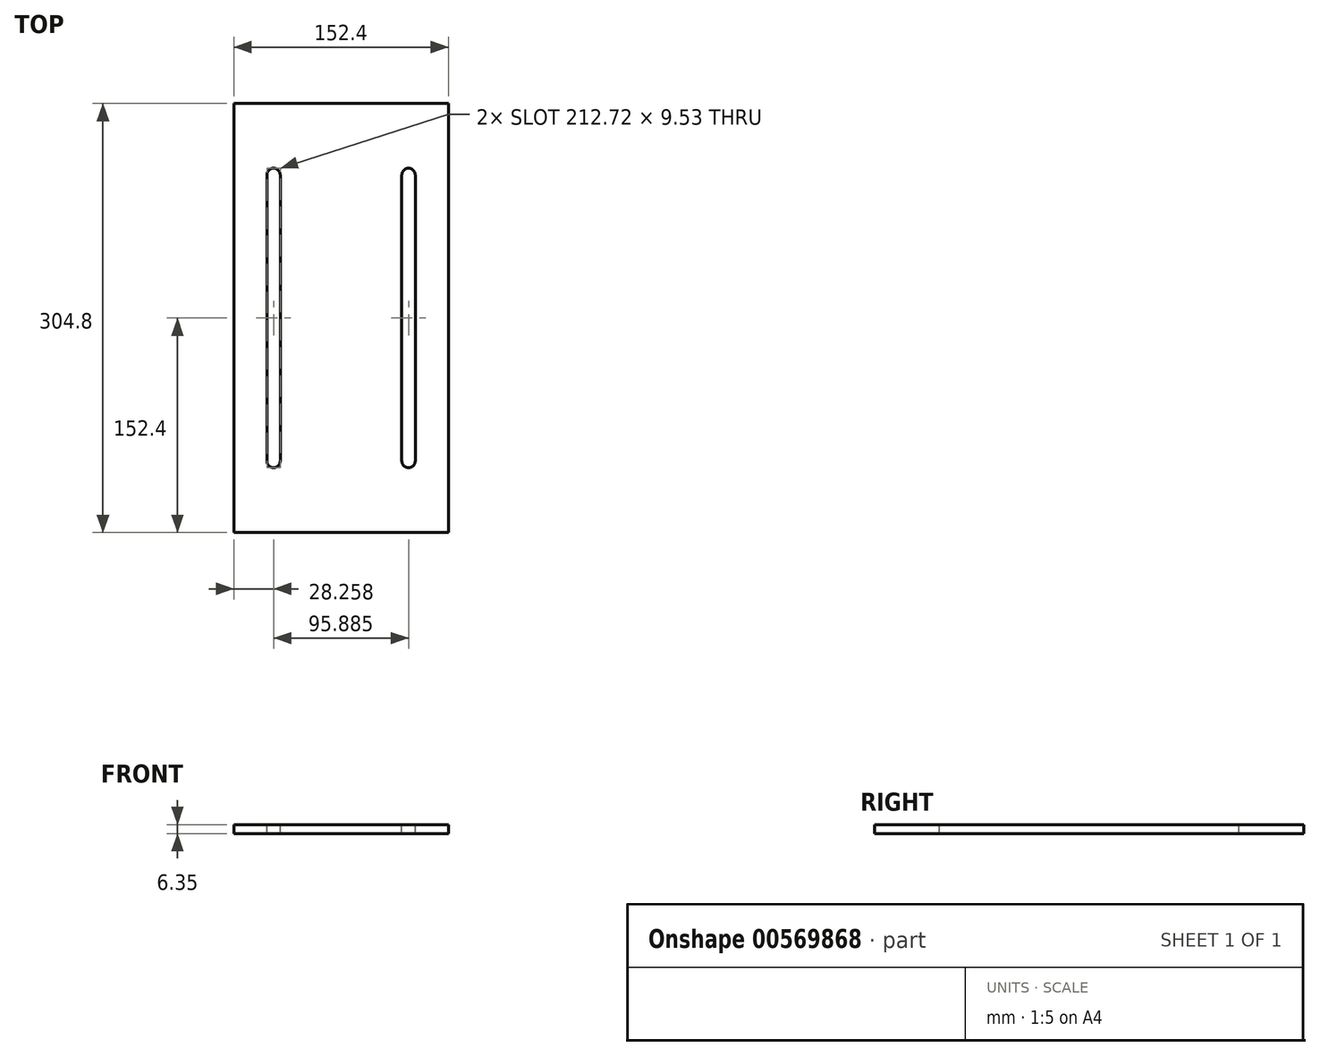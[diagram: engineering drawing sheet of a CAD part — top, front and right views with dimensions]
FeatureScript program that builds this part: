
annotation { "Feature Type Name" : "Feature", "Feature Type Description" : "" }
export const myFeature = defineFeature(function(context is Context, id is Id, definition is map)
    precondition{}
    {
        {
            var Q0;
            Q0=qCreatedBy(makeId("Top.planeOp"),FACE);
            var sketch = newSketch(context, id + "F0", { "sketchPlane" : qUnion([Q0])});
            skLineSegment(sketch, "E0.bottom", {"start": v(0, 0) * mm, "end": v(-152.4, 0) * mm});
            skLineSegment(sketch, "E0.top", {"start": v(0, 304.8) * mm, "end": v(-152.4, 304.8) * mm});
            skLineSegment(sketch, "E0.left", {"start": v(0, 0) * mm, "end": v(0, 304.8) * mm});
            skLineSegment(sketch, "E0.right", {"start": v(-152.4, 0) * mm, "end": v(-152.4, 304.8) * mm});
            skSolve(sketch);
        }
        {
            var Q0;
            Q0 = qSketchRegion(id + "F0", true);
            extrude(context, id + "F1", {"entities" : qUnion([Q0]), "depth" : 6.35 * mm, "offsetDistance" : 25.4 * mm});
        }
        {
            var Q0;
            Q0=makeQuery(id+"F1.opExtrude","CAP_FACE",FACE,{"disambiguationData":[OSD([sQuery(id+"F0.wireOp",EDGE,"E0.bottom"),sQuery(id+"F0.wireOp",EDGE,"E0.top"),sQuery(id+"F0.wireOp",EDGE,"E0.left"),sQuery(id+"F0.wireOp",EDGE,"E0.right")])],"isStart":false});
            var sketch = newSketch(context, id + "F2", { "sketchPlane" : qUnion([Q0])});
            skLineSegment(sketch, "E1.bottom", {"start": v(-128.9, 254) * mm, "end": v(-119.38, 254) * mm});
            skLineSegment(sketch, "E1.top", {"start": v(-128.9, 50.8) * mm, "end": v(-119.38, 50.8) * mm});
            skLineSegment(sketch, "E1.left", {"start": v(-128.9, 254) * mm, "end": v(-128.9, 50.8) * mm});
            skLineSegment(sketch, "E1.right", {"start": v(-119.38, 254) * mm, "end": v(-119.38, 50.8) * mm});
            skLineSegment(sketch, "E2.bottom", {"start": v(-33.02, 254) * mm, "end": v(-23.5, 254) * mm});
            skLineSegment(sketch, "E2.top", {"start": v(-33.02, 50.8) * mm, "end": v(-23.5, 50.8) * mm});
            skLineSegment(sketch, "E2.left", {"start": v(-33.02, 254) * mm, "end": v(-33.02, 50.8) * mm});
            skLineSegment(sketch, "E2.right", {"start": v(-23.5, 254) * mm, "end": v(-23.5, 50.8) * mm});
            skArc(sketch, "E3", {"start": v(-119.38, 254) * mm, "mid": v(-124.14, 258.76) * mm, "end": v(-128.9, 254) * mm});
            skArc(sketch, "E4", {"start": v(-23.5, 254) * mm, "mid": v(-28.26, 258.76) * mm, "end": v(-33.02, 254) * mm});
            skPoint(sketch, "E4.midSnap0", {"position": v(-28.26, 254) * mm});
            skPoint(sketch, "E4.midSnap1", {"position": v(-124.14, 258.76) * mm});
            skArc(sketch, "E5", {"start": v(-128.9, 50.8) * mm, "mid": v(-124.14, 46.04) * mm, "end": v(-119.38, 50.8) * mm});
            skArc(sketch, "E6", {"start": v(-33.02, 50.8) * mm, "mid": v(-28.26, 46.04) * mm, "end": v(-23.5, 50.8) * mm});
            skSolve(sketch);
        }
        {
            var Q0;
            Q0 = qSketchRegion(id + "F2", true);
            extrude(context, id + "F3", {"entities" : qUnion([Q0]), "operationType" : NewBodyOperationType.REMOVE, "oppositeDirection" : true, "depth" : 25.4 * mm, "offsetDistance" : 25.4 * mm});
        }
    });
